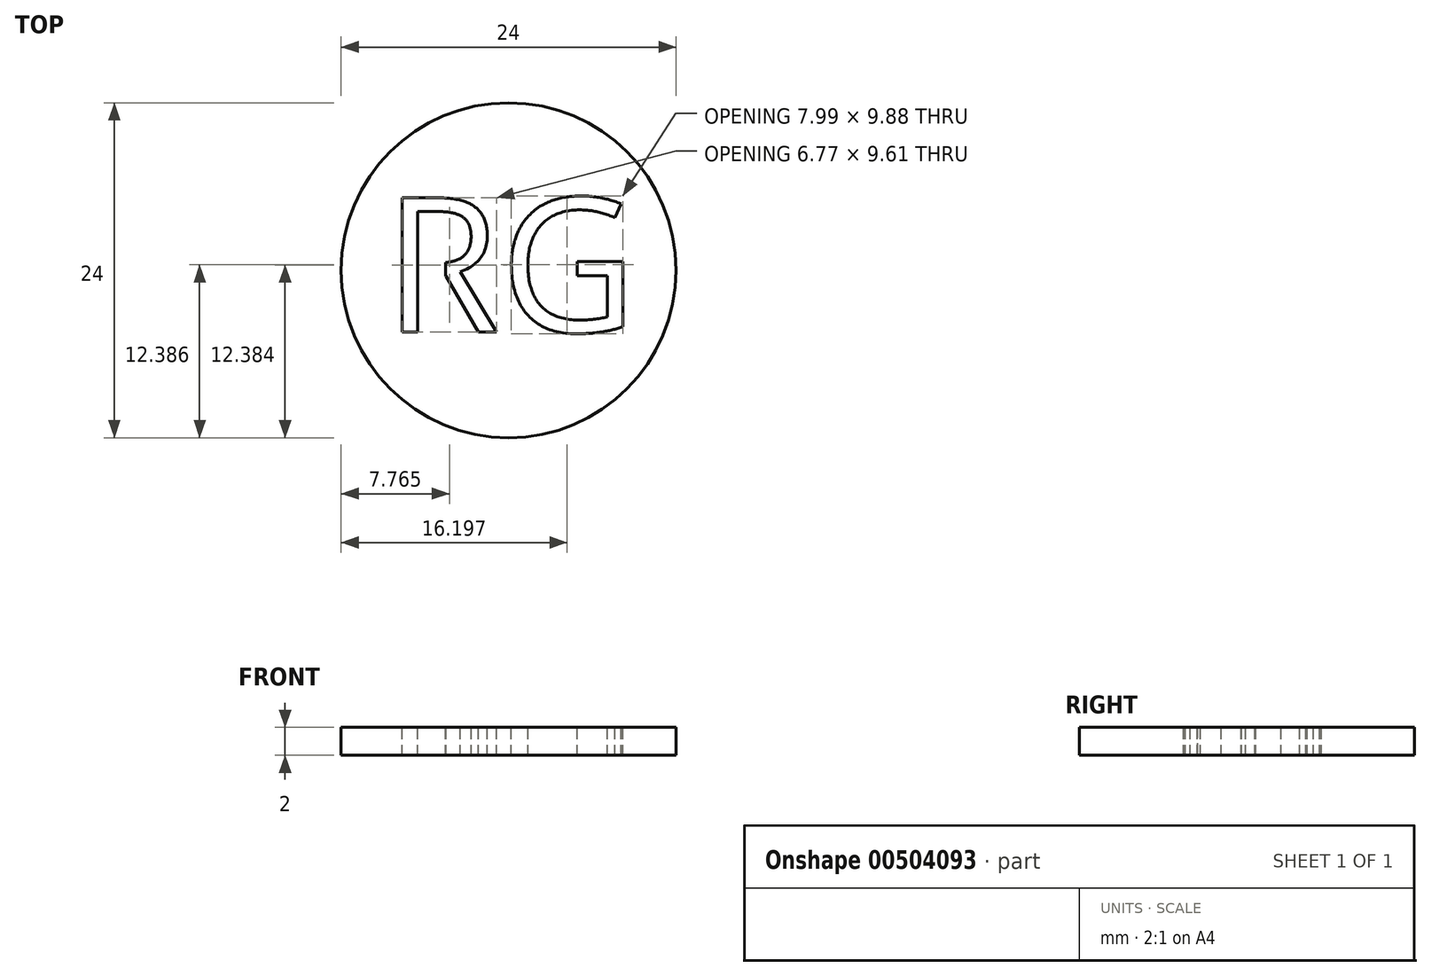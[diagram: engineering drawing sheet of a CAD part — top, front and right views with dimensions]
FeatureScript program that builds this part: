
annotation { "Feature Type Name" : "Feature", "Feature Type Description" : "" }
export const myFeature = defineFeature(function(context is Context, id is Id, definition is map)
    precondition{}
    {
        {
            var Q0;
            Q0=qCreatedBy(makeId("Top.planeOp"),FACE);
            var sketch = newSketch(context, id + "F0", { "sketchPlane" : qUnion([Q0])});
            skCircle(sketch, "E0", {"center": v(0, 0) * mm, "radius": 12 * mm});
            skSolve(sketch);
        }
        {
            var Q0;
            Q0=qSketchRegion(id+"F0",true);
            extrude(context, id + "F1", {"entities" : qUnion([Q0]), "depth" : 2 * mm});
        }
        {
            var Q0;
            Q0=makeQuery(id+"F1.opExtrude","CAP_FACE",FACE,{"disambiguationData":[OSD([sQuery(id+"F0.wireOp",EDGE,"E0")])],"isStart":false});
            var sketch = newSketch(context, id + "F2", { "sketchPlane" : qUnion([Q0])});
            skText(sketch, "E1", { "text": "RG", "fontName": "OpenSans-Regular.ttf"});
            skLineSegment(sketch, "E2.bottom", {"start": v(-6.51, 2.44) * mm, "end": v(-4.5, 2.44) * mm});
            skLineSegment(sketch, "E2.top", {"start": v(-6.51, -1.87) * mm, "end": v(-4.5, -1.87) * mm});
            skLineSegment(sketch, "E2.left", {"start": v(-6.51, 2.44) * mm, "end": v(-6.51, -1.87) * mm});
            skLineSegment(sketch, "E2.right", {"start": v(-4.5, 2.44) * mm, "end": v(-4.5, -1.87) * mm});
            const initialGuessF2  = {"E1": [-0.00894, -0.00442, 1, 0, 0.00969]};
            skSetInitialGuess(sketch, initialGuessF2);
            skSolve(sketch);
        }
        {
            var Q0;
            {var subQ1=sQuery(id+"F2.wireOp",EDGE,"E1.sketch_text.stroke-1");Q0=makeQuery(id+"F2.imprint","IMPRINT",FACE,{"disambiguationData":[TD([[makeQuery(id+"F2.imprint","IMPRINT",EDGE,{"derivedFrom":subQ1}),-1.0]])]});}
            var Q1;
            Q1=makeQuery(id+"F2.imprint","IMPRINT",FACE,{"disambiguationData":[TD([[makeQuery(id+"F2.imprint","IMPRINT",EDGE,{"derivedFrom":sQuery(id+"F2.wireOp",EDGE,"E1.sketch_text.stroke-18")}),-1.0]])]});
            extrude(context, id + "F3", {"entities" : qUnion([Q0, Q1]), "operationType" : NewBodyOperationType.REMOVE, "oppositeDirection" : true, "depth" : 25 * mm});
        }
    });
